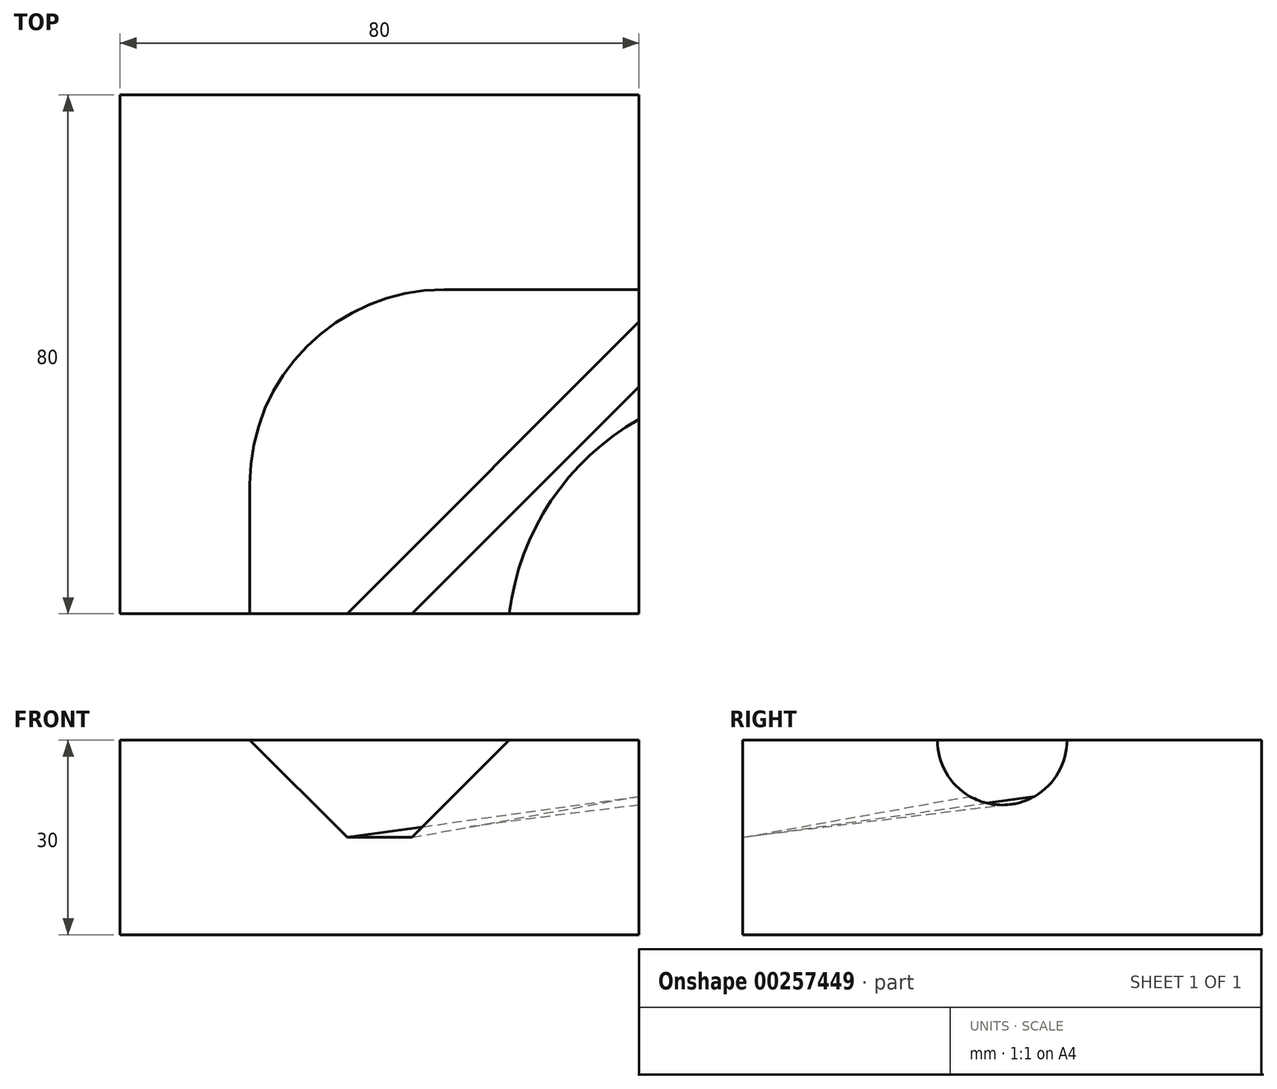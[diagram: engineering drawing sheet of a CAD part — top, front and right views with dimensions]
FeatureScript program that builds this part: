
annotation { "Feature Type Name" : "Feature", "Feature Type Description" : "" }
export const myFeature = defineFeature(function(context is Context, id is Id, definition is map)
    precondition{}
    {
        {
            var Q0;
            Q0=qCreatedBy(makeId("Top.planeOp"),FACE);
            var sketch = newSketch(context, id + "F0", { "sketchPlane" : qUnion([Q0])});
            skLineSegment(sketch, "E0.bottom", {"start": v(0, 0) * mm, "end": v(80, 0) * mm});
            skLineSegment(sketch, "E0.top", {"start": v(0, 80) * mm, "end": v(80, 80) * mm});
            skLineSegment(sketch, "E0.left", {"start": v(0, 0) * mm, "end": v(0, 80) * mm});
            skLineSegment(sketch, "E0.right", {"start": v(80, 0) * mm, "end": v(80, 80) * mm});
            skArc(sketch, "E1", {"start": v(60, 0) * mm, "mid": v(66.43, 17.38) * mm, "end": v(80, 30) * mm});
            skLineSegment(sketch, "E2", {"start": v(80, 50) * mm, "end": v(50, 50) * mm});
            skLineSegment(sketch, "E3", {"start": v(20, 0) * mm, "end": v(20, 20) * mm});
            skArc(sketch, "E4", {"start": v(20, 20) * mm, "mid": v(28.79, 41.21) * mm, "end": v(50, 50) * mm});
            skPoint(sketch, "E5", {"position": v(80, 40) * mm});
            skSolve(sketch);
        }
        {
            var Q0;
            {var subQ1=sQuery(id+"F0.wireOp",EDGE,"E0.top");Q0=makeQuery(id+"F0.imprint","IMPRINT",FACE,{"disambiguationData":[TD([[makeQuery(id+"F0.imprint","IMPRINT",EDGE,{"derivedFrom":subQ1}),-1.0]])]});}
            var Q1;
            {var subQ0=sQuery(id+"F0.wireOp",EDGE,"E1");Q1=makeQuery(id+"F0.imprint","IMPRINT",FACE,{"disambiguationData":[TD([[makeQuery(id+"F0.imprint","IMPRINT",EDGE,{"derivedFrom":subQ0}),1.0]])]});}
            var Q2;
            {var subQ3=sQuery(id+"F0.wireOp",EDGE,"E1");Q2=makeQuery(id+"F0.imprint","IMPRINT",FACE,{"disambiguationData":[TD([[makeQuery(id+"F0.imprint","IMPRINT",EDGE,{"derivedFrom":subQ3}),-1.0]])]});}
            extrude(context, id + "F1", {"entities" : qUnion([Q0, Q1, Q2]), "oppositeDirection" : true, "depth" : 30 * mm});
        }
        {
            var Q0;
            Q0=makeQuery(id+"F1.opExtrude","SWEPT_FACE",FACE,{"disambiguationData":[OSD([sQuery(id+"F0.wireOp",EDGE,"E0.bottom")])]});
            var sketch = newSketch(context, id + "F2", { "sketchPlane" : qUnion([Q0])});
            skLineSegment(sketch, "E6", {"start": v(20, 0) * mm, "end": v(35, -15) * mm});
            skLineSegment(sketch, "E7", {"start": v(60, 0) * mm, "end": v(45, -15) * mm});
            skLineSegment(sketch, "E8", {"start": v(35, -15) * mm, "end": v(45, -15) * mm});
            skSolve(sketch);
        }
        {
            var Q0;
            Q0=makeQuery(id+"F1.opExtrude","SWEPT_FACE",FACE,{"disambiguationData":[OSD([sQuery(id+"F0.wireOp",EDGE,"E0.right")])]});
            var sketch = newSketch(context, id + "F3", { "sketchPlane" : qUnion([Q0])});
            skLineSegment(sketch, "E9.0.0", {"start": v(80, 0) * mm, "end": v(0, 0) * mm});
            skLineSegment(sketch, "E9.0.1", {"start": v(0, 0) * mm, "end": v(0, -30) * mm});
            skLineSegment(sketch, "E9.0.2", {"start": v(0, -30) * mm, "end": v(80, -30) * mm});
            skLineSegment(sketch, "E9.0.3", {"start": v(80, -30) * mm, "end": v(80, 0) * mm});
            skArc(sketch, "E10", {"start": v(30, 0) * mm, "mid": v(40, -10) * mm, "end": v(50, 0) * mm});
            skSolve(sketch);
        }
        {
            var Q0;
            {var subQ1=sQuery(id+"F0.wireOp",EDGE,"E0.top");Q0=makeQuery(id+"F0.imprint","IMPRINT",FACE,{"disambiguationData":[TD([[makeQuery(id+"F0.imprint","IMPRINT",EDGE,{"derivedFrom":subQ1}),-1.0]])]});}
            var sketch = newSketch(context, id + "F4", { "sketchPlane" : qUnion([Q0])});
            skLineSegment(sketch, "E11.0", {"start": v(20, 0) * mm, "end": v(20, 20) * mm});
            skArc(sketch, "E12.0", {"start": v(20, 20) * mm, "mid": v(28.79, 41.21) * mm, "end": v(50, 50) * mm});
            skLineSegment(sketch, "E13.0", {"start": v(80, 50) * mm, "end": v(50, 50) * mm});
            skSolve(sketch);
        }
        {
            var Q1;
            {var subQ0=sQuery(id+"F2.wireOp",EDGE,"E6");Q1=makeQuery(id+"F2.imprint","IMPRINT",FACE,{"disambiguationData":[TD([[makeQuery(id+"F2.imprint","IMPRINT",EDGE,{"derivedFrom":subQ0}),1.0]])]});}
            var Q2;
            {var subQ0=sQuery(id+"F3.wireOp",EDGE,"E10");Q2=makeQuery(id+"F3.imprint","IMPRINT",FACE,{"disambiguationData":[TD([[makeQuery(id+"F3.imprint","IMPRINT",EDGE,{"derivedFrom":subQ0}),1.0]])]});}
            var Q3;
            Q3 = qConstructionFilter(qBodyType(qCreatedBy(id + "F4" ,EDGE), BodyType.WIRE), ConstructionObject.NO);
            var Q4;
            Q4=sQuery(id+"F0.wireOp",EDGE,"E1");
            loft(context, id + "F5", {"operationType" : NewBodyOperationType.REMOVE, "addGuides" : true, "sheetProfilesArray" : [{ "sheetProfileEntities" : qUnion([Q1]) }, { "sheetProfileEntities" : qUnion([Q2]) }], "guidesArray" : [{ "guideEntities" : qUnion([Q3]), "guideDerivativeType" : LoftGuideDerivativeType.DEFAULT, "guideDerivativeMagnitude" : 1 }, { "guideEntities" : qUnion([Q4]), "guideDerivativeType" : LoftGuideDerivativeType.DEFAULT, "guideDerivativeMagnitude" : 1 }]});
        }
    });
